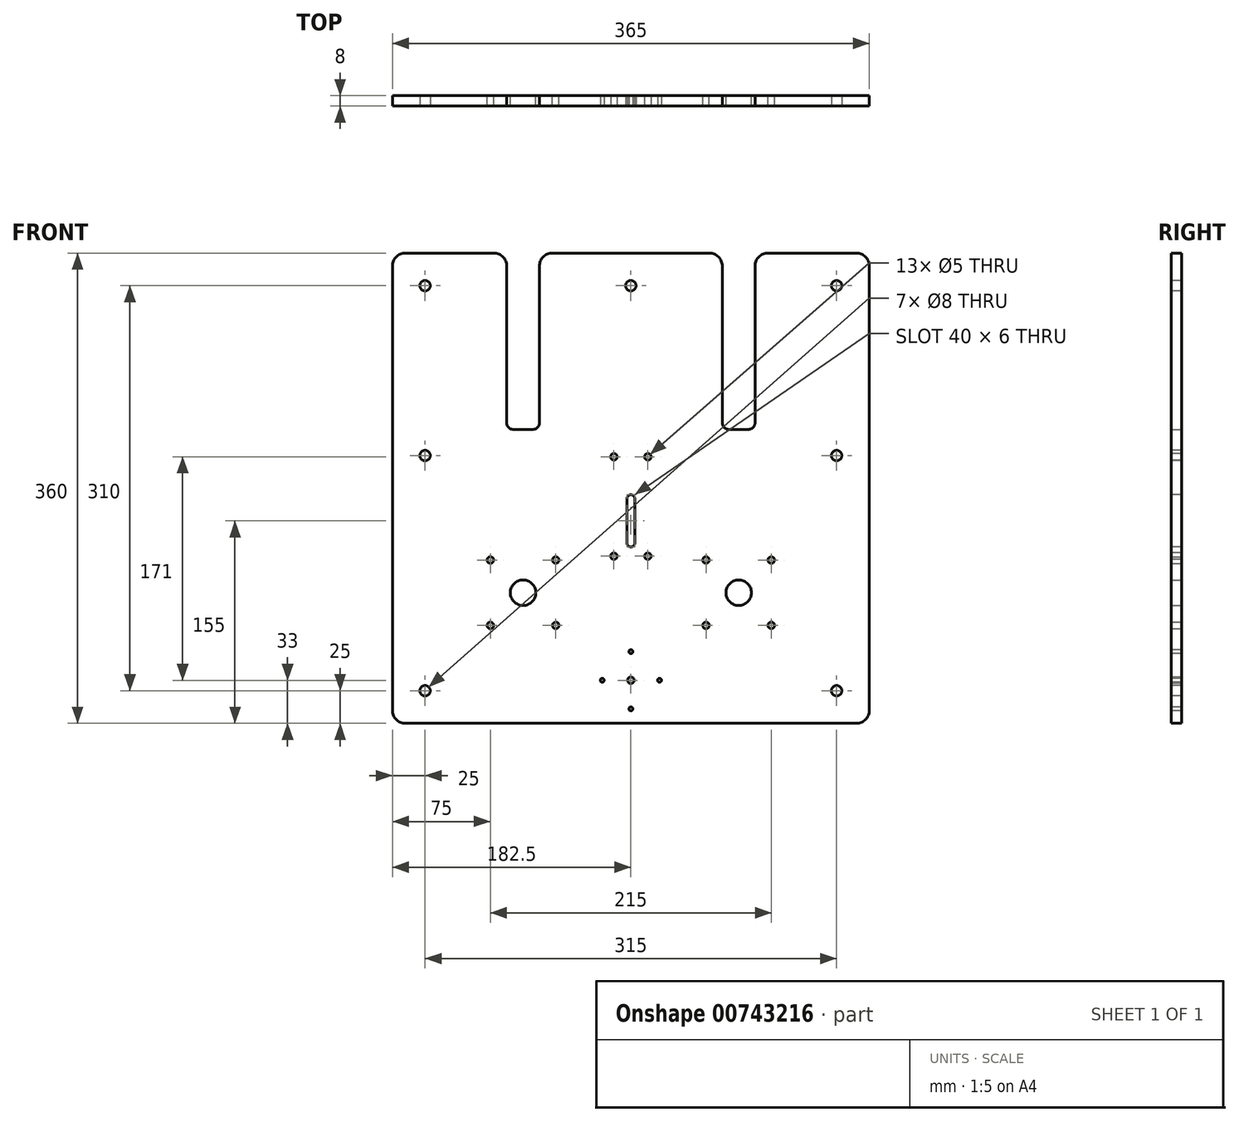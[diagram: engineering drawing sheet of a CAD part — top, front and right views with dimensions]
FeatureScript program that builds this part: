
annotation { "Feature Type Name" : "Feature", "Feature Type Description" : "" }
export const myFeature = defineFeature(function(context is Context, id is Id, definition is map)
    precondition{}
    {
        {
            var Q0;
            Q0=qCreatedBy(makeId("Front.planeOp"),FACE);
            var sketch = newSketch(context, id + "F0", { "sketchPlane" : qUnion([Q0])});
            skLineSegment(sketch, "E0.top", {"start": v(-172.5, -180) * mm, "end": v(172.5, -180) * mm});
            skLineSegment(sketch, "E0.left", {"start": v(-182.5, 170) * mm, "end": v(-182.5, -170) * mm});
            skLineSegment(sketch, "E0.right", {"start": v(182.5, 170) * mm, "end": v(182.5, -170) * mm});
            skPoint(sketch, "E0.middle", {"position": v(0, 0) * mm});
            skLineSegment(sketch, "E1", {"start": v(-216.45, 0) * mm, "end": v(222.01, 0) * mm, "construction": true});
            skLineSegment(sketch, "E2", {"start": v(0, 234.86) * mm, "end": v(0, -196.31) * mm, "construction": true});
            skPoint(sketch, "E2.startSnap0", {"position": v(0, 180) * mm});
            skLineSegment(sketch, "E3.bottom", {"start": v(-82.5, 80) * mm, "end": v(82.5, 80) * mm, "construction": true});
            skLineSegment(sketch, "E3.top", {"start": v(-82.5, -80) * mm, "end": v(82.5, -80) * mm, "construction": true});
            skLineSegment(sketch, "E3.left", {"start": v(-82.5, 80) * mm, "end": v(-82.5, -80) * mm, "construction": true});
            skLineSegment(sketch, "E3.right", {"start": v(82.5, 80) * mm, "end": v(82.5, -80) * mm, "construction": true});
            skCircle(sketch, "E4", {"center": v(82.5, 80) * mm, "radius": 80 * mm, "construction": true});
            skCircle(sketch, "E5", {"center": v(-82.5, 80) * mm, "radius": 80 * mm, "construction": true});
            skCircle(sketch, "E6", {"center": v(-82.5, -80) * mm, "radius": 80 * mm, "construction": true});
            skCircle(sketch, "E7", {"center": v(82.5, -80) * mm, "radius": 80 * mm, "construction": true});
            skLineSegment(sketch, "E8", {"start": v(172.5, 180) * mm, "end": v(105, 180) * mm});
            skLineSegment(sketch, "E9", {"start": v(95, 170) * mm, "end": v(95, 50) * mm});
            skLineSegment(sketch, "E10", {"start": v(90, 45) * mm, "end": v(75, 45) * mm});
            skLineSegment(sketch, "E11", {"start": v(70, 50) * mm, "end": v(70, 170) * mm});
            skLineSegment(sketch, "E12", {"start": v(60, 180) * mm, "end": v(-60, 180) * mm});
            skLineSegment(sketch, "E13", {"start": v(-70, 170) * mm, "end": v(-70, 50) * mm});
            skLineSegment(sketch, "E14", {"start": v(-75, 45) * mm, "end": v(-90, 45) * mm});
            skLineSegment(sketch, "E15", {"start": v(-95, 50) * mm, "end": v(-95, 170) * mm});
            skLineSegment(sketch, "E16", {"start": v(-105, 180) * mm, "end": v(-172.5, 180) * mm});
            skPoint(sketch, "E17.visualSharp", {"position": v(-182.5, 180) * mm});
            skArc(sketch, "E17.filletArc", {"start": v(-172.5, 180) * mm, "mid": v(-179.57, 177.07) * mm, "end": v(-182.5, 170) * mm});
            skPoint(sketch, "E18.visualSharp", {"position": v(182.5, 180) * mm});
            skArc(sketch, "E18.filletArc", {"start": v(182.5, 170) * mm, "mid": v(179.57, 177.07) * mm, "end": v(172.5, 180) * mm});
            skPoint(sketch, "E19.visualSharp", {"position": v(182.5, -180) * mm});
            skArc(sketch, "E19.filletArc", {"start": v(172.5, -180) * mm, "mid": v(179.57, -177.07) * mm, "end": v(182.5, -170) * mm});
            skPoint(sketch, "E20.visualSharp", {"position": v(-182.5, -180) * mm});
            skArc(sketch, "E20.filletArc", {"start": v(-182.5, -170) * mm, "mid": v(-179.57, -177.07) * mm, "end": v(-172.5, -180) * mm});
            skPoint(sketch, "E21.visualSharp", {"position": v(-95, 180) * mm});
            skArc(sketch, "E21.filletArc", {"start": v(-95, 170) * mm, "mid": v(-97.93, 177.07) * mm, "end": v(-105, 180) * mm});
            skPoint(sketch, "E22.visualSharp", {"position": v(-70, 180) * mm});
            skArc(sketch, "E22.filletArc", {"start": v(-60, 180) * mm, "mid": v(-67.07, 177.07) * mm, "end": v(-70, 170) * mm});
            skPoint(sketch, "E23.visualSharp", {"position": v(70, 180) * mm});
            skArc(sketch, "E23.filletArc", {"start": v(70, 170) * mm, "mid": v(67.07, 177.07) * mm, "end": v(60, 180) * mm});
            skPoint(sketch, "E24.visualSharp", {"position": v(95, 180) * mm});
            skArc(sketch, "E24.filletArc", {"start": v(105, 180) * mm, "mid": v(97.93, 177.07) * mm, "end": v(95, 170) * mm});
            skCircle(sketch, "E25", {"center": v(-82.5, -80) * mm, "radius": 9.75 * mm});
            skCircle(sketch, "E26", {"center": v(82.5, -80) * mm, "radius": 9.75 * mm});
            skLineSegment(sketch, "E27.bottom", {"start": v(-107.5, -55) * mm, "end": v(-57.5, -55) * mm, "construction": true});
            skLineSegment(sketch, "E27.top", {"start": v(-107.5, -105) * mm, "end": v(-57.5, -105) * mm, "construction": true});
            skLineSegment(sketch, "E27.left", {"start": v(-107.5, -55) * mm, "end": v(-107.5, -105) * mm, "construction": true});
            skLineSegment(sketch, "E27.right", {"start": v(-57.5, -55) * mm, "end": v(-57.5, -105) * mm, "construction": true});
            skLineSegment(sketch, "E28.bottom", {"start": v(57.5, -55) * mm, "end": v(107.5, -55) * mm, "construction": true});
            skLineSegment(sketch, "E28.top", {"start": v(57.5, -105) * mm, "end": v(107.5, -105) * mm, "construction": true});
            skLineSegment(sketch, "E28.left", {"start": v(57.5, -55) * mm, "end": v(57.5, -105) * mm, "construction": true});
            skLineSegment(sketch, "E28.right", {"start": v(107.5, -55) * mm, "end": v(107.5, -105) * mm, "construction": true});
            skCircle(sketch, "E29", {"center": v(-107.5, -55) * mm, "radius": 2.5 * mm});
            skCircle(sketch, "E30", {"center": v(-107.5, -105) * mm, "radius": 2.5 * mm});
            skCircle(sketch, "E31", {"center": v(-57.5, -105) * mm, "radius": 2.5 * mm});
            skCircle(sketch, "E32", {"center": v(-57.5, -55) * mm, "radius": 2.5 * mm});
            skCircle(sketch, "E33", {"center": v(57.5, -55) * mm, "radius": 2.5 * mm});
            skCircle(sketch, "E34", {"center": v(57.5, -105) * mm, "radius": 2.5 * mm});
            skCircle(sketch, "E35", {"center": v(107.5, -105) * mm, "radius": 2.5 * mm});
            skCircle(sketch, "E36", {"center": v(107.5, -55) * mm, "radius": 2.5 * mm});
            skPoint(sketch, "E37.visualSharp", {"position": v(95, 45) * mm});
            skArc(sketch, "E37.filletArc", {"start": v(90, 45) * mm, "mid": v(93.54, 46.46) * mm, "end": v(95, 50) * mm});
            skPoint(sketch, "E38.visualSharp", {"position": v(70, 45) * mm});
            skArc(sketch, "E38.filletArc", {"start": v(70, 50) * mm, "mid": v(71.46, 46.46) * mm, "end": v(75, 45) * mm});
            skPoint(sketch, "E39.visualSharp", {"position": v(-95, 45) * mm});
            skArc(sketch, "E39.filletArc", {"start": v(-95, 50) * mm, "mid": v(-93.54, 46.46) * mm, "end": v(-90, 45) * mm});
            skPoint(sketch, "E40.visualSharp", {"position": v(-70, 45) * mm});
            skArc(sketch, "E40.filletArc", {"start": v(-75, 45) * mm, "mid": v(-71.46, 46.46) * mm, "end": v(-70, 50) * mm});
            skSolve(sketch);
        }
        {
            var Q0;
            Q0=makeQuery(id+"F0.imprint","IMPRINT",FACE,{"disambiguationData":[TD([[makeQuery(id+"F0.imprint","IMPRINT",EDGE,{"derivedFrom":sQuery(id+"F0.wireOp",EDGE,"E0.top")}),1.0]])]});
            extrude(context, id + "F1", {"entities" : qUnion([Q0]), "depth" : 8 * mm, "offsetDistance" : 25 * mm});
        }
        {
            var Q0;
            Q0=makeQuery(id+"F1.opExtrude","CAP_FACE",FACE,{"disambiguationData":[OSD([sQuery(id+"F0.wireOp",EDGE,"E0.top"),sQuery(id+"F0.wireOp",EDGE,"E0.left"),sQuery(id+"F0.wireOp",EDGE,"E0.right"),sQuery(id+"F0.wireOp",EDGE,"E8"),sQuery(id+"F0.wireOp",EDGE,"E9"),sQuery(id+"F0.wireOp",EDGE,"E10"),sQuery(id+"F0.wireOp",EDGE,"E11"),sQuery(id+"F0.wireOp",EDGE,"E12"),sQuery(id+"F0.wireOp",EDGE,"E13"),sQuery(id+"F0.wireOp",EDGE,"E14"),sQuery(id+"F0.wireOp",EDGE,"E15"),sQuery(id+"F0.wireOp",EDGE,"E16"),sQuery(id+"F0.wireOp",EDGE,"E17.filletArc"),sQuery(id+"F0.wireOp",EDGE,"E18.filletArc"),sQuery(id+"F0.wireOp",EDGE,"E19.filletArc"),sQuery(id+"F0.wireOp",EDGE,"E20.filletArc"),sQuery(id+"F0.wireOp",EDGE,"E21.filletArc"),sQuery(id+"F0.wireOp",EDGE,"E22.filletArc"),sQuery(id+"F0.wireOp",EDGE,"E23.filletArc"),sQuery(id+"F0.wireOp",EDGE,"E24.filletArc")])],"isStart":false});
            var sketch = newSketch(context, id + "F2", { "sketchPlane" : qUnion([Q0])});
            skLineSegment(sketch, "E41.0", {"start": v(0, 234.86) * mm, "end": v(0, -196.31) * mm, "construction": true});
            skLineSegment(sketch, "E42.0", {"start": v(-216.45, 0) * mm, "end": v(222.01, 0) * mm, "construction": true});
            skLineSegment(sketch, "E43.bottom", {"start": v(-157.5, 155) * mm, "end": v(157.5, 155) * mm, "construction": true});
            skLineSegment(sketch, "E43.top", {"start": v(-157.5, -155) * mm, "end": v(157.5, -155) * mm, "construction": true});
            skLineSegment(sketch, "E43.left", {"start": v(-157.5, 155) * mm, "end": v(-157.5, -155) * mm, "construction": true});
            skLineSegment(sketch, "E43.right", {"start": v(157.5, 155) * mm, "end": v(157.5, -155) * mm, "construction": true});
            skPoint(sketch, "E43.middle", {"position": v(0, 0) * mm});
            skCircle(sketch, "E44", {"center": v(157.5, 155) * mm, "radius": 4 * mm});
            skCircle(sketch, "E45", {"center": v(157.5, -155) * mm, "radius": 4 * mm});
            skCircle(sketch, "E46", {"center": v(-157.5, -155) * mm, "radius": 4 * mm});
            skCircle(sketch, "E47", {"center": v(-157.5, 155) * mm, "radius": 4 * mm});
            skCircle(sketch, "E48", {"center": v(0, 155) * mm, "radius": 4 * mm});
            skLineSegment(sketch, "E49", {"start": v(157.5, 25) * mm, "end": v(-157.5, 25) * mm, "construction": true});
            skCircle(sketch, "E50", {"center": v(157.5, 25) * mm, "radius": 4 * mm});
            skCircle(sketch, "E51", {"center": v(-157.5, 25) * mm, "radius": 4 * mm});
            skLineSegment(sketch, "E52.bottom", {"start": v(0, -5) * mm, "end": v(0, -5) * mm});
            skLineSegment(sketch, "E52.top", {"start": v(0, -45) * mm, "end": v(0, -45) * mm});
            skLineSegment(sketch, "E52.left", {"start": v(-3, -8) * mm, "end": v(-3, -42) * mm});
            skLineSegment(sketch, "E52.right", {"start": v(3, -8) * mm, "end": v(3, -42) * mm});
            skPoint(sketch, "E52.middle", {"position": v(0, -25) * mm});
            skPoint(sketch, "E53.visualSharp", {"position": v(-3, -5) * mm});
            skArc(sketch, "E53.filletArc", {"start": v(0, -5) * mm, "mid": v(-2.12, -5.88) * mm, "end": v(-3, -8) * mm});
            skPoint(sketch, "E54.visualSharp", {"position": v(3, -5) * mm});
            skArc(sketch, "E54.filletArc", {"start": v(3, -8) * mm, "mid": v(2.12, -5.88) * mm, "end": v(0, -5) * mm});
            skPoint(sketch, "E55.visualSharp", {"position": v(3, -45) * mm});
            skArc(sketch, "E55.filletArc", {"start": v(0, -45) * mm, "mid": v(2.12, -44.12) * mm, "end": v(3, -42) * mm});
            skPoint(sketch, "E56.visualSharp", {"position": v(-3, -45) * mm});
            skArc(sketch, "E56.filletArc", {"start": v(-3, -42) * mm, "mid": v(-2.12, -44.12) * mm, "end": v(0, -45) * mm});
            skPoint(sketch, "E57.middle", {"position": v(0, -147) * mm});
            skCircle(sketch, "E58", {"center": v(0, -147) * mm, "radius": 2.5 * mm});
            skCircle(sketch, "E59", {"center": v(-13, 24) * mm, "radius": 2.5 * mm});
            skCircle(sketch, "E60", {"center": v(13, 24) * mm, "radius": 2.5 * mm});
            skCircle(sketch, "E61", {"center": v(-13, -52) * mm, "radius": 2.5 * mm});
            skCircle(sketch, "E62", {"center": v(13, -52) * mm, "radius": 2.5 * mm});
            skLineSegment(sketch, "E63.bottom", {"start": v(13, 24) * mm, "end": v(-13, 24) * mm, "construction": true});
            skLineSegment(sketch, "E63.top", {"start": v(13, -52) * mm, "end": v(-13, -52) * mm, "construction": true});
            skLineSegment(sketch, "E63.left", {"start": v(13, 24) * mm, "end": v(13, -52) * mm, "construction": true});
            skLineSegment(sketch, "E63.right", {"start": v(-13, 24) * mm, "end": v(-13, -52) * mm, "construction": true});
            skCircle(sketch, "E64.cCircle", {"center": v(0, -147) * mm, "radius": 15.5 * mm, "construction": true});
            skLineSegment(sketch, "E64.seed", {"start": v(21.92, -147) * mm, "end": v(0, -125.08) * mm, "construction": true});
            skLineSegment(sketch, "E64.pattern.0.1.0", {"start": v(0, -125.08) * mm, "end": v(-21.92, -147) * mm, "construction": true});
            skLineSegment(sketch, "E64.pattern.0.2.0", {"start": v(-21.92, -147) * mm, "end": v(0, -168.92) * mm, "construction": true});
            skLineSegment(sketch, "E64.pattern.0.3.0", {"start": v(0, -168.92) * mm, "end": v(21.92, -147) * mm, "construction": true});
            skPoint(sketch, "E64.midPoint", {"position": v(10.96, -136.04) * mm, "construction": true});
            skCircle(sketch, "E65", {"center": v(0, -125.08) * mm, "radius": 1.5 * mm});
            skCircle(sketch, "E66.cCircle", {"center": v(0, -147) * mm, "radius": 21 * mm, "construction": true});
            skLineSegment(sketch, "E66.seed", {"start": v(0, -117.3) * mm, "end": v(-29.7, -147) * mm, "construction": true});
            skLineSegment(sketch, "E66.pattern.0.1.0", {"start": v(-29.7, -147) * mm, "end": v(0, -176.7) * mm, "construction": true});
            skLineSegment(sketch, "E66.pattern.0.2.0", {"start": v(0, -176.7) * mm, "end": v(29.7, -147) * mm, "construction": true});
            skLineSegment(sketch, "E66.pattern.0.3.0", {"start": v(29.7, -147) * mm, "end": v(0, -117.3) * mm, "construction": true});
            skPoint(sketch, "E66.midPoint", {"position": v(-14.85, -132.15) * mm, "construction": true});
            skCircle(sketch, "E67", {"center": v(0, -168.92) * mm, "radius": 1.5 * mm});
            skCircle(sketch, "E68", {"center": v(-21.92, -147) * mm, "radius": 1.5 * mm});
            skCircle(sketch, "E69", {"center": v(21.92, -147) * mm, "radius": 1.5 * mm});
            skSolve(sketch);
        }
        {
            var Q0;
            Q0 = qSketchRegion(id + "F2", true);
            extrude(context, id + "F3", {"entities" : qUnion([Q0]), "operationType" : NewBodyOperationType.REMOVE, "flatOperationType" : FlatOperationType.REMOVE, "endBound" : BoundingType.UP_TO_NEXT, "oppositeDirection" : true, "depth" : 25 * mm, "offsetDistance" : 25 * mm, "domain" : OperationDomain.MODEL});
        }
    });
